# Revit family: Desk-Teknion-CHDH_High_Adjustable_Desk-R2021
name_source: partatom
category: Furniture
units: mm (PartAtom-declared; Revit-internal decimal feet)

## family parameters
Always vertical = Yes
Cut with Voids When Loaded = No
OmniClass Number = 23.40.20.00
OmniClass Title = General Furniture and Specialties
Room Calculation Point = No
Shared = Yes
Work Plane-Based = No

## types (4) — shared parameters
Assembly Code = E2020200
Manufacturer = Teknion
Manufacturer Fax = 416.661.4586
Part Number = CHDH
Product Documentation Link = https://www.teknion.com
Product Line = Chronicle
Product Page URL = https://www.teknion.com
Series = Chronicle
Sustainability Data = https://www.teknion.com
URL = www.teknion.com
Unit Weight URL = http://www.teknion.com
Warranty = http://www.teknion.com
zero-valued in all types: Default Elevation

## per-type parameters (varying)
| type | Depth | Description | Model | Modesty Height |
| 28" Depth, Partial Modesty Height , Inset Position | 28 " | Height Adjustable Desk, 28" Depth, Partial Modesty Height , Inset Position | CHDH28_A | 10 " |
| 28" Depth, Mid Modesty Height , Inset Position | 28 " | Height Adjustable Desk, 28" Depth, Mid Modesty Height , Inset Position | CHDH28_C | 20.25 " |
| 34" Depth, Partial Modesty Height , Inset Position | 34 " | Height Adjustable Desk, 34" Depth, Partial Modesty Height , Inset Position | CHDH34_A | 10 " |
| 34" Depth, Mid Modesty Height , Inset Position | 34 " | Height Adjustable Desk, 34" Depth, Mid Modesty Height , Inset Position | CHDH34_C | 20.25 " |

## geometry (parser evidence)
native form markers: Sweep x3
no freeform markers — native parametric forms only
